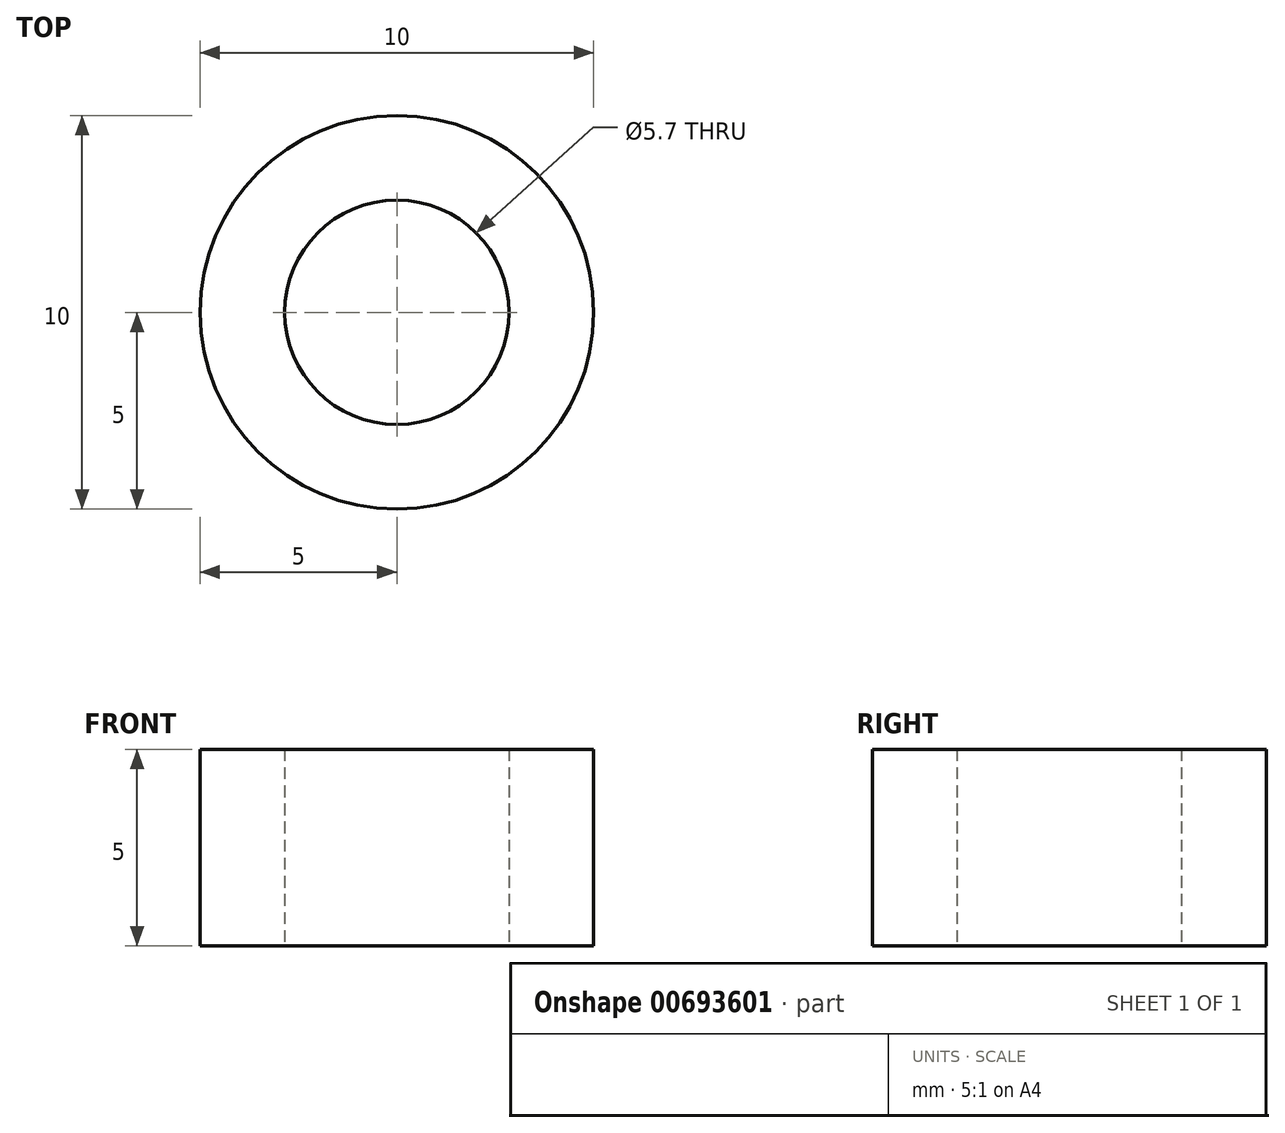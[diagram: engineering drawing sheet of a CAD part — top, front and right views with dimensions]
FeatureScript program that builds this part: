
annotation { "Feature Type Name" : "Feature", "Feature Type Description" : "" }
export const myFeature = defineFeature(function(context is Context, id is Id, definition is map)
    precondition{}
    {
        {
            var Q0;
            Q0=qCreatedBy(makeId("Top.planeOp"),FACE);
            var sketch = newSketch(context, id + "F0", { "sketchPlane" : qUnion([Q0])});
            skCircle(sketch, "E0", {"center": v(0, 0) * mm, "radius": 5 * mm});
            skCircle(sketch, "E1", {"center": v(0, 0) * mm, "radius": 2.85 * mm});
            skSolve(sketch);
        }
        {
            var Q0;
            Q0=makeQuery(id+"F0.imprint","IMPRINT",FACE,{"disambiguationData":[TD([[makeQuery(id+"F0.imprint","IMPRINT",EDGE,{"derivedFrom":sQuery(id+"F0.wireOp",EDGE,"E0")}),1.0]])]});
            extrude(context, id + "F1", {"entities" : qUnion([Q0]), "depth" : 5 * mm, "offsetDistance" : 25 * mm});
        }
    });
